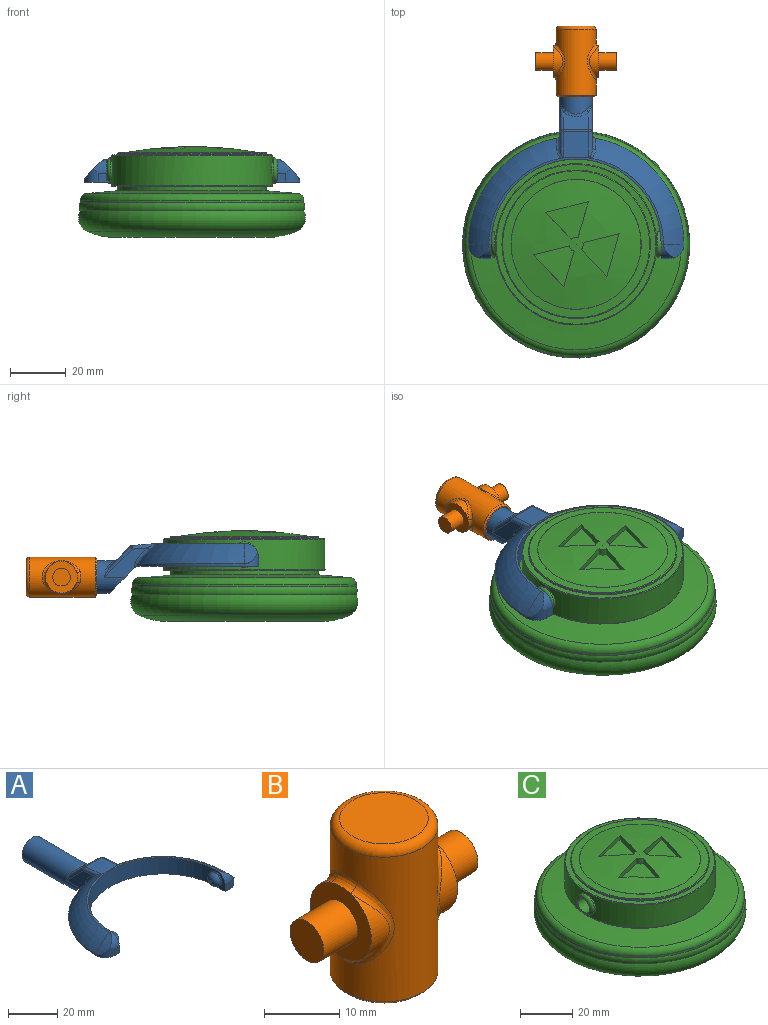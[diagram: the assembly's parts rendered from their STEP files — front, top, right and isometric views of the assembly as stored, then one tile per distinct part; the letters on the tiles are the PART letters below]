
ASSEMBLY  parts=3 mates=2
PART A: 48 faces, bbox 77.3x80.8x18.2 mm
  f0: plane 11.99x9.83mm, normal (0,-0.71,-0.71), area 141.5mm2, adj f1,f2,f9,f30,f43,f46
  f1: plane 15.39x10.49mm, normal (-1,0,0), area 63.5mm2, adj f0,f30,f32,f36,f46,f47
  f2: plane 15.39x10.49mm, normal (1,0,0), area 63.5mm2, adj f0,f30,f34,f39,f43,f44
  f3: plane 9.14x6.37mm, normal (0,0.71,0.71), area 67.6mm2, adj f35,f36,f39,f40
  f4: cylinder r=38.61mm len=37.99mm, axis (0,0,-1), area 42.6mm2, adj f6,f9,f17,f46,f47
  f5: torus R=19.3mm, axis (0,0,-1), area 507.8mm2, adj f10,f11,f12,f29,f42,f44
  f6: torus R=19.3mm, axis (0,0,-1), area 507.8mm2, adj f4,f11,f15,f28,f45,f47
  f7: cylinder r=30.48mm len=60.96mm, axis (0,0,-1), area 746.6mm2, adj f8,f9,f11,f14,f21,f24
  f8: plane 8.13x5.08mm, normal (-1,0,0), area 19.9mm2, adj f7,f9,f13,f19,f24
  f9: plane 77.22x43.73mm, normal (0,0,-1), area 956.2mm2, adj f0,f4,f7,f8,f10,f13,f14,f16
  f10: cylinder r=38.61mm len=37.99mm, axis (0,0,-1), area 42.6mm2, adj f5,f9,f20,f43,f44
  f11: plane 62.55x30.95mm, normal (0,0,1), area 75mm2, adj f5,f6,f7,f18,f19,f27
  f12: cylinder r=22.71mm len=7.33mm, axis (0,1,0), area 24.8mm2, adj f5,f19,f20
  f13: plane 3.05x3.05mm, normal (0,-1,0), area 9.3mm2, adj f8,f9,f19,f20
  f14: plane 8.13x5.08mm, normal (1,0,0), area 19.9mm2, adj f7,f9,f16,f18,f21
  f15: cylinder r=22.71mm len=7.33mm, axis (0,1,0), area 24.8mm2, adj f6,f17,f18
  f16: plane 3.05x3.05mm, normal (0,-1,0), area 9.3mm2, adj f9,f14,f17,f18
  f17: cylinder r=5.08mm len=5.08mm, axis (0,0,-1), area 21.9mm2, adj f4,f9,f15,f16,f18
  f18: cylinder r=5.08mm len=5.08mm, axis (-1,0,0), area 21.9mm2, adj f11,f14,f15,f16,f17
  f19: cylinder r=5.08mm len=5.08mm, axis (-1,0,0), area 21.9mm2, adj f8,f11,f12,f13,f20
  f20: cylinder r=5.08mm len=5.08mm, axis (0,0,-1), area 21.9mm2, adj f9,f10,f12,f13,f19
  f21: cylinder r=3.17mm len=6.35mm, axis (-1,0,0), area 12.7mm2, adj f7,f14,f23
  f22: plane 1.27x1.27mm, normal (1,0,0), area 1.3mm2, adj f23
  f23: torus R=0.64mm, axis (1,0,0), area 56.5mm2, adj f21,f22
  f24: cylinder r=3.17mm len=6.35mm, axis (1,0,0), area 12.7mm2, adj f7,f8,f26
  f25: plane 1.27x1.27mm, normal (-1,0,0), area 1.3mm2, adj f26
  f26: torus R=0.64mm, axis (-1,0,0), area 56.5mm2, adj f24,f25
  f27: plane 9.86x9.36mm, normal (0,0.09,1), area 85.6mm2, adj f11,f28,f29,f32,f34,f35,f42,f45
  f28: plane 1.04x0.17mm, normal (0,-1,0), area 0mm2, adj f6,f27,f45
  f29: plane 1.04x0.17mm, normal (0,-1,0), area 0mm2, adj f5,f27,f42
  f30: cylinder r=5.84mm len=33.01mm, axis (0,-1,0), area 1029.7mm2, adj f0,f1,f2,f31,f38,f40,f41
  f31: plane 11.68x11.68mm, normal (0,1,0), area 107.2mm2, adj f30
  f32: cylinder r=1.27mm len=9.13mm, axis (0,-1,0.09), area 14.4mm2, adj f1,f27,f33,f45
  f33: sphere r=1.27mm, area 1.5mm2, adj f32,f35,f36
  f34: cylinder r=1.27mm len=9.13mm, axis (0,1,-0.09), area 14.4mm2, adj f2,f27,f37,f42
  f35: cylinder r=1.27mm len=9.14mm, axis (-1,0,0), area 8.1mm2, adj f3,f27,f33,f37
  f36: cylinder r=1.27mm len=10.91mm, axis (0,-0.71,0.71), area 23.1mm2, adj f1,f3,f33,f38
  f37: sphere r=1.27mm, area 1.5mm2, adj f34,f35,f39
  f38: bspline ~4.55x2.75mm, area 2.3mm2, adj f30,f36,f40
  f39: cylinder r=1.27mm len=10.91mm, axis (0,0.71,-0.71), area 23.1mm2, adj f2,f3,f37,f41
  f40: bspline ~9.14x2.56mm, area 10.7mm2, adj f3,f30,f38,f41
  f41: bspline ~5.23x3.53mm, area 2.3mm2, adj f30,f39,f40
  f42: bspline ~4.62x3.14mm, area 5.2mm2, adj f5,f27,f29,f34,f44
  f43: cylinder r=1.27mm len=1.74mm, axis (0,0,-1), area 1.9mm2, adj f0,f2,f9,f10,f44
  f44: bspline ~8.6x7.86mm, area 11.9mm2, adj f2,f5,f10,f42,f43
  f45: bspline ~4.62x3.14mm, area 5.2mm2, adj f6,f27,f28,f32,f47
  f46: cylinder r=1.27mm len=1.74mm, axis (0,0,-1), area 1.9mm2, adj f0,f1,f4,f9,f47
  f47: bspline ~8.6x7.86mm, area 11.9mm2, adj f1,f4,f6,f45,f46
PART B: 25 faces, bbox 28.9x15.5x25.4 mm
  f0: cylinder r=5.71mm len=10.81mm, axis (-1,0,0), area 26.2mm2, adj f5,f15
  f1: cylinder r=5.71mm len=10.81mm, axis (-1,0,0), area 26.2mm2, adj f8,f11
  f2: cylinder r=7.14mm len=23.5mm, axis (0,0,-1), area 763.2mm2, adj f9,f10,f11,f12,f13,f14,f15,f16
  f3: plane 11.75x11.75mm, normal (0,0,1), area 108.4mm2, adj f17
  f4: plane 13.02x13.02mm, normal (0,0,-1), area 16.3mm2, adj f22,f24
  f5: plane 11.46x11.46mm, normal (1,0,0), area 70.9mm2, adj f0,f6,f13,f16,f18
  f6: cylinder r=5.71mm len=10.81mm, axis (-1,0,0), area 26.2mm2, adj f5,f14
  f7: cylinder r=5.71mm len=10.81mm, axis (-1,0,0), area 26.2mm2, adj f8,f10
  f8: plane 11.46x11.46mm, normal (-1,0,0), area 70.9mm2, adj f1,f7,f9,f12,f20
  f9: bspline ~4.64x1.73mm, area 6.5mm2, adj f2,f8,f10,f11
  f10: bspline ~13.62x4.91mm, area 20.7mm2, adj f2,f7,f9,f12
  f11: bspline ~13.6x4.87mm, area 20.7mm2, adj f1,f2,f9,f12
  f12: bspline ~4.64x1.73mm, area 6.5mm2, adj f2,f8,f10,f11
  f13: bspline ~4.64x1.73mm, area 6.5mm2, adj f2,f5,f14,f15
  f14: bspline ~13.62x4.91mm, area 20.7mm2, adj f2,f6,f13,f16
  f15: bspline ~13.6x4.87mm, area 20.7mm2, adj f0,f2,f13,f16
  f16: bspline ~4.64x1.73mm, area 6.5mm2, adj f2,f5,f14,f15
  f17: torus R=5.87mm, axis (0,0,1), area 83.8mm2, adj f2,f3
  f18: cylinder r=3.17mm len=6.35mm, axis (-1,0,0), area 126.7mm2, adj f5,f19
  f19: plane 6.35x6.35mm, normal (1,0,0), area 31.7mm2, adj f18
  f20: cylinder r=3.17mm len=6.35mm, axis (1,0,0), area 126.7mm2, adj f8,f21
  f21: plane 6.35x6.35mm, normal (-1,0,0), area 31.7mm2, adj f20
  f22: cylinder r=6.1mm len=22.86mm, axis (0,0,-1), area 875.6mm2, adj f4,f23
  f23: plane 12.19x12.19mm, normal (0,0,-1), area 116.7mm2, adj f22
  f24: cone r=7.14mm half-angle=45deg, axis (0,0,1), area 38.5mm2, adj f2,f4
PART C: 41 faces, bbox 96.2x96.2x32.5 mm
  f0: cylinder r=28.87mm len=57.73mm, axis (0,0,-1), area 1814.4mm2, adj f31,f32,f37,f38
  f1: sphere r=135.39mm, area 1392.9mm2, adj f15,f16,f17,f18,f20,f21,f22,f23
  f2: plane 39.33x39.33mm, normal (0,0,-1), area 1214.6mm2, adj f3
  f3: torus R=20.12mm, axis (0,0,-1), area 1429.3mm2, adj f2,f4
  f4: torus R=27.74mm, axis (0,0,-1), area 3542.1mm2, adj f3,f5
  f5: torus R=35.36mm, axis (0,0,-1), area 2180.1mm2, adj f4,f6
  f6: torus R=37.35mm, axis (0,0,-1), area 734.6mm2, adj f5,f7
  f7: cylinder r=40.06mm len=80.11mm, axis (0,0,-1), area 213.3mm2, adj f6,f14
  f8: cone r=26.57mm half-angle=85deg, axis (0,0,-1), area 2265mm2, adj f9,f14
  f9: cylinder r=26.57mm len=53.14mm, axis (0,0,-1), area 265mm2, adj f8,f10
  f10: plane 57.23x57.23mm, normal (0,0,-1), area 354.5mm2, adj f9,f37
  f11: plane 57.23x57.23mm, normal (0,0,1), area 354.5mm2, adj f12,f38
  f12: cylinder r=26.57mm len=53.14mm, axis (0,0,-1), area 92.3mm2, adj f11,f39
  f13: cone r=26.57mm half-angle=87deg, axis (0,0,-1), area 475.4mm2, adj f39,f40
  f14: torus R=37.52mm, axis (0,0,1), area 928.6mm2, adj f7,f8
  f15: cylinder r=2.54mm len=2.52mm, axis (0,0,1), area 6.7mm2, adj f1,f16,f18,f19
  f16: plane 9.63x9.23mm, normal (0.72,0.69,0), area 29mm2, adj f1,f15,f17,f19
  f17: plane 15.24x4.43mm, normal (-0.96,0.28,0), area 28mm2, adj f1,f16,f18,f19
  f18: plane 12.95x3.18mm, normal (0.24,-0.97,0), area 29mm2, adj f1,f15,f17,f19
  f19: plane 15.24x13.66mm, normal (0,0,1), area 105.7mm2, adj f15,f16,f17,f18
  f20: cylinder r=2.54mm len=2.52mm, axis (0,0,1), area 6.7mm2, adj f1,f21,f23,f24
  f21: plane 12.8x3.72mm, normal (-0.96,0.28,0), area 29mm2, adj f1,f20,f22,f24
  f22: plane 15.42x3.78mm, normal (0.24,-0.97,0), area 28mm2, adj f1,f21,f23,f24
  f23: plane 9.63x9.23mm, normal (0.72,0.69,0), area 29mm2, adj f1,f20,f22,f24
  f24: plane 15.42x13.41mm, normal (0,0,1), area 105.7mm2, adj f20,f21,f22,f23
  f25: plane 12.8x3.72mm, normal (-0.96,0.28,0), area 29mm2, adj f1,f26,f28,f29
  f26: cylinder r=2.54mm len=2.52mm, axis (0,0,1), area 6.7mm2, adj f1,f25,f27,f29
  f27: plane 12.95x3.18mm, normal (0.24,-0.97,0), area 29mm2, adj f1,f26,f28,f29
  f28: plane 11.46x10.99mm, normal (0.72,0.69,0), area 28mm2, adj f1,f25,f27,f29
  f29: plane 14.71x14.64mm, normal (0,0,1), area 105.7mm2, adj f25,f26,f27,f28
  f30: plane 6.6x6.6mm, normal (1,0,0), area 2.6mm2, adj f35,f36
  f31: cylinder r=4.57mm len=9.14mm, axis (-1,0,0), area 15.1mm2, adj f0,f35
  f32: cylinder r=4.57mm len=9.14mm, axis (-1,0,0), area 15.1mm2, adj f0,f34
  f33: plane 6.6x6.6mm, normal (-1,0,0), area 2.6mm2, adj f34,f36
  f34: torus R=3.3mm, axis (1,0,0), area 51.5mm2, adj f32,f33
  f35: torus R=3.3mm, axis (1,0,0), area 51.5mm2, adj f30,f31
  f36: cylinder r=3.17mm len=60.96mm, axis (1,0,0), area 1216.1mm2, adj f30,f33
  f37: torus R=28.61mm, axis (0,0,1), area 72.1mm2, adj f0,f10
  f38: torus R=28.61mm, axis (0,0,-1), area 72.1mm2, adj f0,f11
  f39: torus R=26.31mm, axis (0,0,1), area 64.2mm2, adj f12,f13
  f40: torus R=23.29mm, axis (0,0,1), area 4.5mm2, adj f1,f13
PLACE A t=(32.34,27.52,20.85)mm
PLACE B rot(axis=(-1,0,0),90deg) t=(32.34,80.3,16.88)mm
PLACE C t=(32.34,27.52,33.52)mm
MATE revolute A.f24 <-> C.f31  axis (-1,0,0) through (62.82,27.52,24.92)mm
MATE revolute B.f2 <-> A.f30  axis (0,-1,0) through (32.34,103.16,16.88)mm
